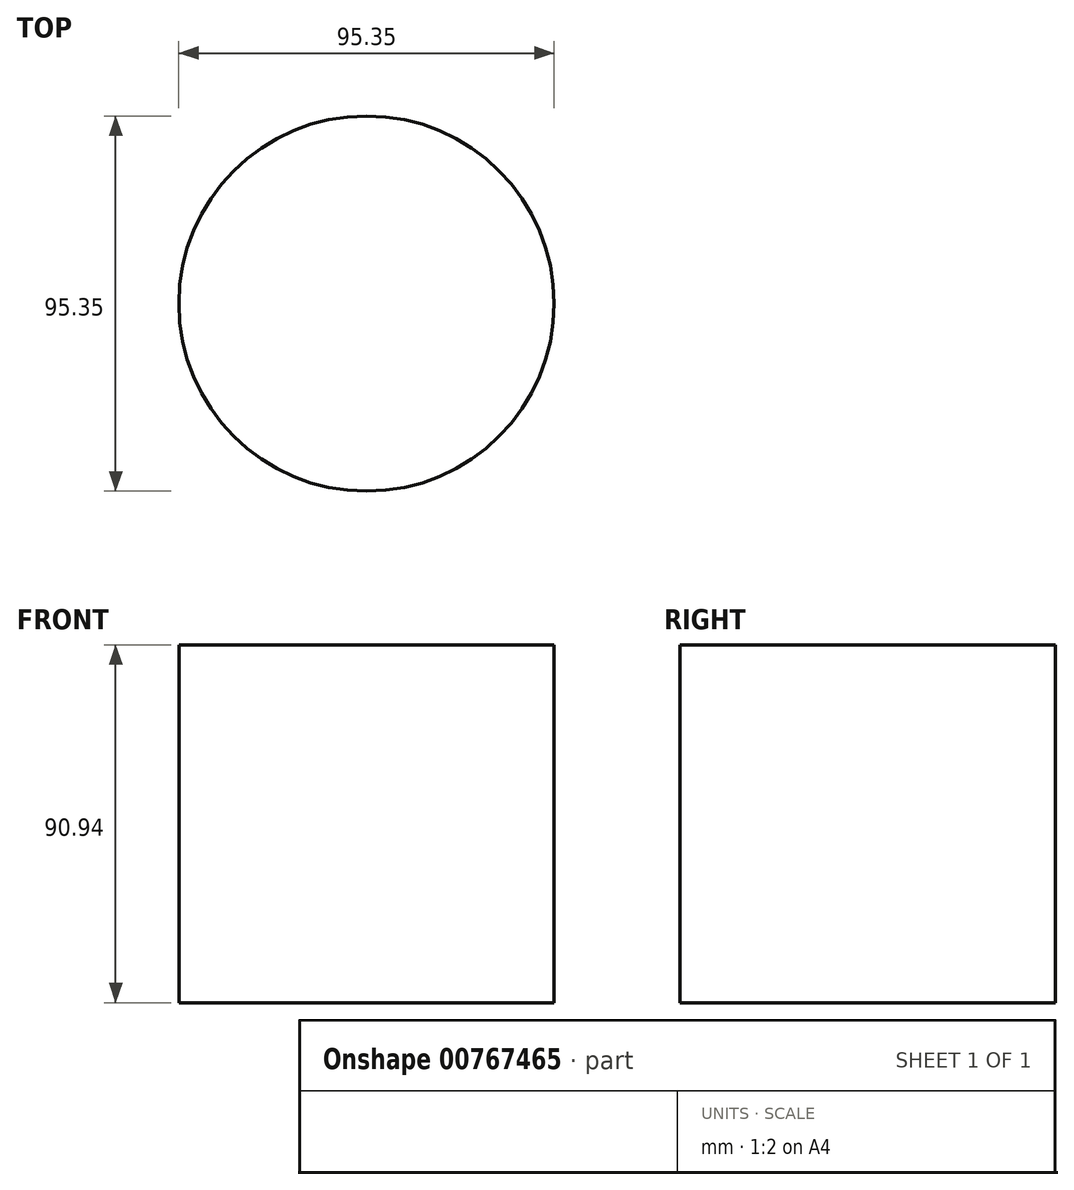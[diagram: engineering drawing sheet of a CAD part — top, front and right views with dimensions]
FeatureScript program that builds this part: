
annotation { "Feature Type Name" : "Feature", "Feature Type Description" : "" }
export const myFeature = defineFeature(function(context is Context, id is Id, definition is map)
    precondition{}
    {
        {
            var Q0;
            Q0=qCreatedBy(makeId("Top.planeOp"),FACE);
            var sketch = newSketch(context, id + "F0", { "sketchPlane" : qUnion([Q0])});
            skCircle(sketch, "E0", {"center": v(-54.85, 29.99) * mm, "radius": 47.67 * mm});
            skSolve(sketch);
        }
        {
            var Q0;
            Q0=makeQuery(id+"F0.imprint","IMPRINT",FACE,{"disambiguationData":[TD([[makeQuery(id+"F0.imprint","IMPRINT",EDGE,{"derivedFrom":sQuery(id+"F0.wireOp",EDGE,"E0")}),1.0]])]});
            extrude(context, id + "F1", {"entities" : qUnion([Q0]), "endBound" : BoundingType.SYMMETRIC, "depth" : 90.93 * mm, "offsetDistance" : 25.4 * mm});
        }
    });
